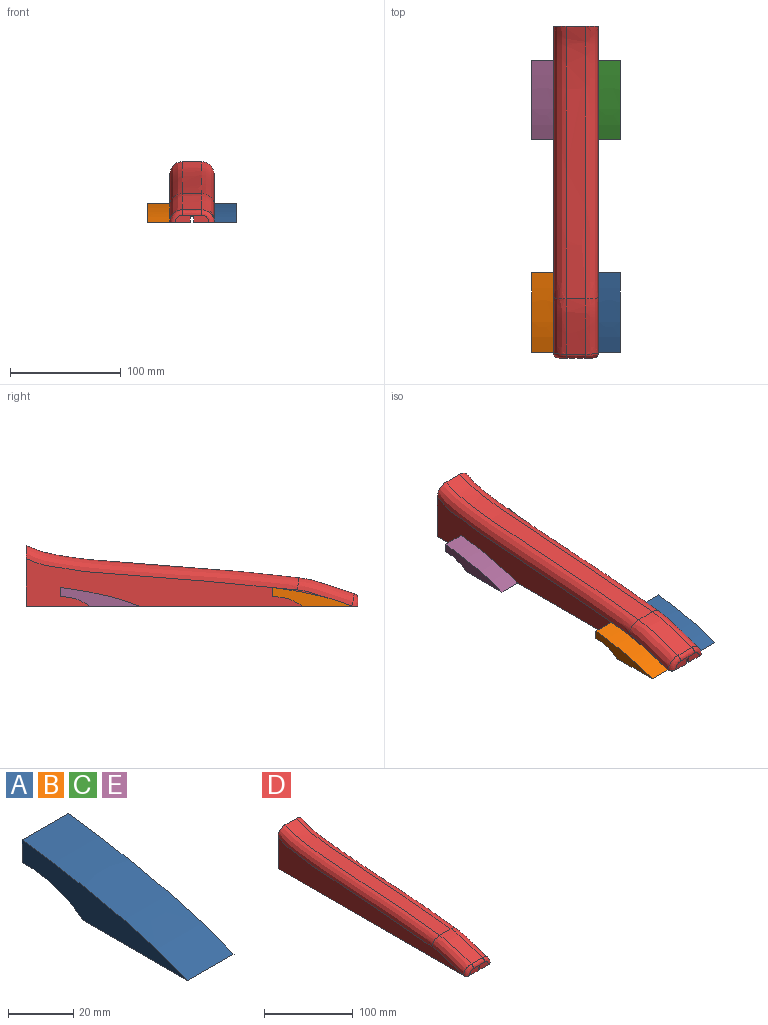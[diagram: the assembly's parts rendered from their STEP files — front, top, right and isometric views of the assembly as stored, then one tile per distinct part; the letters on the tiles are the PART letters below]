
ASSEMBLY  parts=5 mates=4
PART A: 6 faces, bbox 20x72.1x16.9 mm
  f0: plane 20x8.45mm, normal (0,1,0), area 168.9mm2, adj f2,f3,f4,f5
  f1: plane 45.35x20mm, normal (0,0,-1), area 907mm2, adj f2,f3,f4,f5
  f2: plane 72.06x16.89mm, normal (1,0,0), area 567.5mm2, adj f0,f1,f4,f5
  f3: plane 72.06x16.89mm, normal (-1,0,0), area 567.5mm2, adj f0,f1,f4,f5
  f4: extruded ~72.06x20mm, area 1484.5mm2, adj f0,f1,f2,f3
  f5: cylinder r=41.07mm len=26.71mm, axis (1,0,0), area 571.7mm2, adj f0,f1,f2,f3
PART B: same geometry as A
PART C: same geometry as A
PART D: 20 faces, bbox 43.2x306.9x58.7 mm
  f0: plane 300.22x18.72mm, normal (0,0,-1), area 5545.9mm2, adj f1,f3,f6,f10,f14,f17
  f1: plane 30.02x6.48mm, normal (0,-1,0), area 161.9mm2, adj f0,f5,f14,f15,f16,f17,f18,f19
  f2: plane 294.99x42.97mm, normal (1,0,0), area 6783.9mm2, adj f5,f6,f12,f13
  f3: plane 294.99x42.97mm, normal (-1,0,0), area 6783.9mm2, adj f0,f6,f10,f11
  f4: extruded ~246.52x28.93mm, area 4428.4mm2, adj f6,f9,f11,f13
  f5: plane 300.19x18.69mm, normal (0,0,-1), area 5545.6mm2, adj f1,f2,f6,f12,f16,f18
  f6: plane 57.79x43.17mm, normal (0,1,0), area 1801.1mm2, adj f0,f2,f3,f4,f5,f7,f11,f13
  f7: cylinder r=10mm len=50mm, axis (0,1,0), area 3141.6mm2, adj f6,f8
  f8: plane 20x20mm, normal (0,1,0), area 314.2mm2, adj f7
  f9: extruded ~50.12x17.79mm, area 930.1mm2, adj f4,f10,f12,f15
  f10: bspline ~56.51x26.63mm, area 910.1mm2, adj f0,f3,f9,f11,f14
  f11: bspline ~251.42x40.27mm, area 4314.7mm2, adj f3,f4,f6,f10
  f12: bspline ~56.51x26.63mm, area 910.1mm2, adj f2,f5,f9,f13,f16
  f13: bspline ~251.58x40.3mm, area 4315.2mm2, adj f2,f4,f6,f12
  f14: bspline ~11.19x11.11mm, area 100.8mm2, adj f0,f1,f10,f15
  f15: bspline ~17.79x4.73mm, area 111.6mm2, adj f1,f9,f14,f16
  f16: bspline ~11.19x11.11mm, area 100.8mm2, adj f1,f5,f12,f15
  f17: plane 300x5mm, normal (1,0,0), area 1500mm2, adj f0,f1,f6,f19
  f18: plane 300x5mm, normal (-1,0,0), area 1500mm2, adj f1,f5,f6,f19
  f19: plane 300x3mm, normal (0,0,-1), area 900mm2, adj f1,f6,f17,f18
PART E: same geometry as A
PLACE A t=(3.56,-117.47,11.12)mm
PLACE B t=(-56.44,-117.47,11.12)mm
PLACE C t=(3.56,74.67,11.12)mm
PLACE D t=(-16.44,85.6,-9.79)mm
PLACE E t=(-56.44,74.67,11.12)mm
MATE fastened A.f3 <-> D.f2  axis (-1,0,0) through (3.56,-148.19,-17.23)mm
MATE fastened E.f2 <-> D.f3  axis (1,0,0) through (-36.44,89.3,-17.23)mm
MATE fastened C.f3 <-> D.f2  axis (-1,0,0) through (3.56,89.3,-17.23)mm
MATE fastened B.f2 <-> D.f3  axis (1,0,0) through (-36.44,-148.19,-17.23)mm
